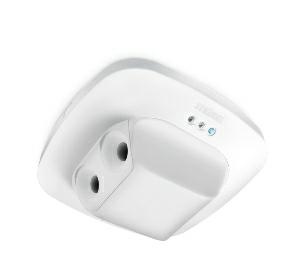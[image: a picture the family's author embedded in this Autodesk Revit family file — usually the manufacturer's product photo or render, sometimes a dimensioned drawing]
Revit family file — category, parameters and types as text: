
# Revit family: dual_us_007843
name_source: partatom
category: Elektroinstallationen
revit_build: Autodesk Revit 2016 (Build: 20190508_0715(x64)
units: mm (PartAtom-declared; Revit-internal decimal feet)

## family parameters
Basisbauteil = Fläche
Beim Laden mit Abzugskörper schneiden = Nein
Bemaßung runder Anschluss = Durchmesser verwenden
Beschriftungsausrichtung beibehalten = Nein
Gemeinsam genutzt = Nein
Raumberechnungspunkt = Nein
Teiletyp = Normal

## types (1)
- Dual US
    Apparent Load = 0 VA
    Beschreibung = Type: Presence detector; Dimensions (L x W x H): 73 x 120 x 120 mm; Mains power supply: 220 – 240 V / 50 – 60 Hz; Sensor Technology: Ultrasonic; Application, place: Indoors; Application, room: corridor / aisle, Indoors; Installation site: ceiling; Installation: Concealed wiring; Electronic scalability: Yes; Mechanical scalability: No; Mounting height: 2,50 – 3,50 m; Optimum mounting height: 2,8 m; Detection angle: 360 °; Sneak-by guard: Yes; Reach, radial: 20 x 3 m (60 m²); Reach, tangential: 20 x 3 m (60 m²); Twilight setting TEACH: Yes; Twilight setting: 10 – 1000 lx; Time setting: 30 sec – 30 min; Constant-lighting control: No; Basic light level function: No; Functions: Normal / test mode, Semi-/fully automatic, Pushbutton / switch mode, Manual ON / ON-OFF; Settings via: Remote control, DIP switches, Potentiometers, Smart Remote; With remote control: Yes; Interconnection: Yes; Type of interconnection: Master/slave, Master/master; IP-rating: IP20; Material: Plastic; Ambient temperature: -25 – 55 °C; Colour: white; Colour, RAL: 9010; Manufacturer's Warranty: 5 years; Version: COM1; PU1, EAN: 4007841007843
    Height = 0 mm  [stored 0 ft]
    Hersteller = Steinel
    Length = 73 mm
    Maximum range = 10.098 m
    ModVariant = Nein
    Modell = 007843
    Mounting Place = Ceiling
    Mounting Type = Recessed
    Number of Poles = 1
    OnlyDefault = Ja
    Power Factor = 1
    Product Name = Dual US
    Product group = Presence detector
    ProductGroupID = 4
    Protection Class = Protection class
    Protection Degree = IP 20
    RlxData = <blob elided: 160741 chars, md5=2de1e273>
    Sensor characteristics = Stretched
    Sensor type = Passive (infrared)
    SensorDataFile = <blob elided: 184890 chars, md5=e609621d>
    Type of entry = Motion
    Typenbild = produkt1_007843.jpg
    Typenkommentare = Product without accessories
    URL = http://relux.com
    VarID = ---
    Voltage = 0 V
    Vorgabe-Ansicht = 1800 mm
    Weight = 0.00 kg
    Width = 120 mm  [stored 0.393701 ft]

note: [stored X ft] marks values corroborated as IEEE doubles in the binary element streams (Revit-internal decimal feet)

## geometry (parser evidence)
native form markers: Sweep x16
no freeform markers — native parametric forms only
